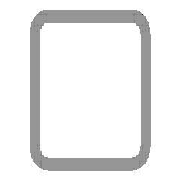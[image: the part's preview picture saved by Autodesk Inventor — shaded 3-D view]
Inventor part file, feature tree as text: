
AUTODESK INVENTOR PART (.ipt)
format: ipt  version: 2021 (Build 250183000, 183)  size: 144,384 bytes
history: native  units: mm (DEFAULTED — no unit token found)
features: other x5, sketch x3, extrude x1, split x1, plane x1
ambient origin geometry x8: Origin, YZ Plane, XZ Plane, XY Plane, X Axis, Y Axis, Z Axis, Center Point
bodies: Solid1 (feature_tree)
feature tree (11):
  parser-record x1  (decoder bookkeeping rows leaked as tree rows — omitted from the tree; the rows remain in map.json)
  other  "Driven Length"
  other  "Plano inicial"
  other  "Plano final"
  extrude  "Corpo"  TaperAngle=0.0deg  [1 undecoded]
  other  "Plano de trabalho4"
  split  "Dividir1"
  sketch  "Esboço"  dims[d11=50.8mm d12=4.7625mm d13=-15.698063mm d14=2236.067977mm d15=25.4mm d16=25.4mm d17=9.525mm d18=90.0deg d19=2251.766041mm]
  sketch  "Sketch3"  dims[d3=2251.766041mm d4=0.0mm]
  plane  "Work Plane3"
  sketch  "Sketch4"  dims[d10=50.8mm]
note: 1 required parameter value undecoded (feature->parameter linkage not recoverable at this tier; creation-order binding heuristic only, values carry confidence <= 0.55)
